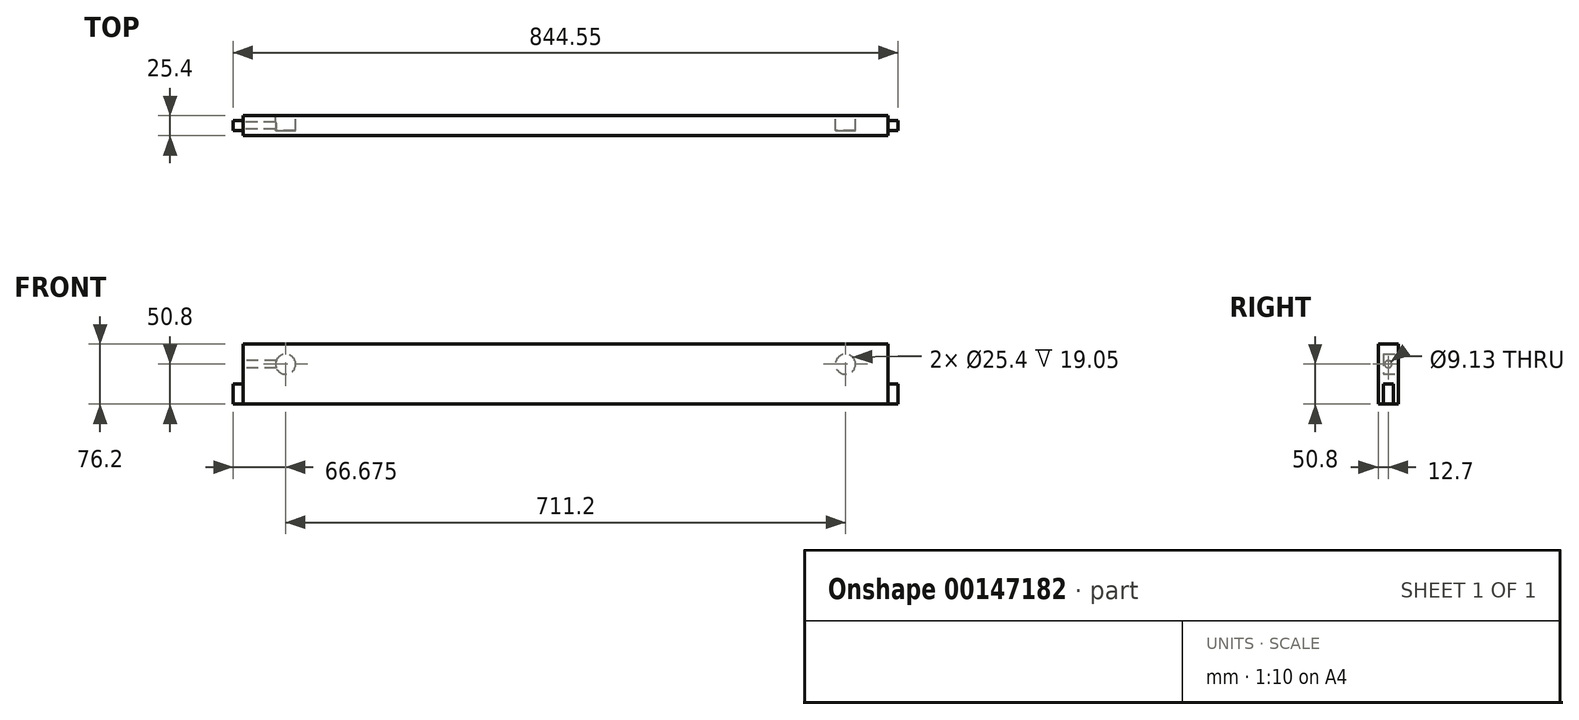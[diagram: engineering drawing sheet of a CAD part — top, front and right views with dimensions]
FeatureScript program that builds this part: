
annotation { "Feature Type Name" : "Feature", "Feature Type Description" : "" }
export const myFeature = defineFeature(function(context is Context, id is Id, definition is map)
    precondition{}
    {
        {
            var Q0;
            Q0=qCreatedBy(makeId("Front.planeOp"),FACE);
            var sketch = newSketch(context, id + "F0", { "sketchPlane" : qUnion([Q0])});
            skLineSegment(sketch, "E0.bottom", {"start": v(0, 0) * mm, "end": v(844.55, 0) * mm});
            skLineSegment(sketch, "E0.top", {"start": v(0, 76.2) * mm, "end": v(844.55, 76.2) * mm});
            skLineSegment(sketch, "E0.left", {"start": v(0, 0) * mm, "end": v(0, 76.2) * mm});
            skLineSegment(sketch, "E0.right", {"start": v(844.55, 0) * mm, "end": v(844.55, 76.2) * mm});
            skSolve(sketch);
        }
        {
            var Q0;
            Q0=makeQuery(id+"F0.imprint","IMPRINT",FACE,{"disambiguationData":[TD([[makeQuery(id+"F0.imprint","IMPRINT",EDGE,{"derivedFrom":sQuery(id+"F0.wireOp",EDGE,"E0.bottom")}),1.0]])]});
            extrude(context, id + "F1", {"entities" : qUnion([Q0]), "depth" : 25.4 * mm});
        }
        {
            var Q0;
            Q0=makeQuery(id+"F1.opExtrude","CAP_FACE",FACE,{"disambiguationData":[OSD([sQuery(id+"F0.wireOp",EDGE,"E0.bottom"),sQuery(id+"F0.wireOp",EDGE,"E0.top"),sQuery(id+"F0.wireOp",EDGE,"E0.left"),sQuery(id+"F0.wireOp",EDGE,"E0.right")])],"isStart":false});
            var sketch = newSketch(context, id + "F2", { "sketchPlane" : qUnion([Q0])});
            skLineSegment(sketch, "E1.bottom", {"start": v(0, 76.2) * mm, "end": v(12.7, 76.2) * mm});
            skLineSegment(sketch, "E1.top", {"start": v(0, 25.4) * mm, "end": v(12.7, 25.4) * mm});
            skLineSegment(sketch, "E1.left", {"start": v(0, 76.2) * mm, "end": v(0, 25.4) * mm});
            skLineSegment(sketch, "E1.right", {"start": v(12.7, 76.2) * mm, "end": v(12.7, 25.4) * mm});
            skLineSegment(sketch, "E2.bottom", {"start": v(831.85, 76.2) * mm, "end": v(844.55, 76.2) * mm});
            skLineSegment(sketch, "E2.top", {"start": v(831.85, 25.4) * mm, "end": v(844.55, 25.4) * mm});
            skLineSegment(sketch, "E2.left", {"start": v(831.85, 76.2) * mm, "end": v(831.85, 25.4) * mm});
            skLineSegment(sketch, "E2.right", {"start": v(844.55, 76.2) * mm, "end": v(844.55, 25.4) * mm});
            skSolve(sketch);
        }
        {
            var Q0;
            Q0=makeQuery(id+"F2.imprint","IMPRINT",FACE,{"disambiguationData":[TD([[makeQuery(id+"F2.imprint","IMPRINT",EDGE,{"derivedFrom":sQuery(id+"F2.wireOp",EDGE,"E1.bottom")}),-1.0]])]});
            var Q1;
            Q1=makeQuery(id+"F2.imprint","IMPRINT",FACE,{"disambiguationData":[TD([[makeQuery(id+"F2.imprint","IMPRINT",EDGE,{"derivedFrom":sQuery(id+"F2.wireOp",EDGE,"E2.bottom")}),-1.0]])]});
            extrude(context, id + "F3", {"entities" : qUnion([Q0, Q1]), "operationType" : NewBodyOperationType.REMOVE, "endBound" : BoundingType.THROUGH_ALL, "oppositeDirection" : true, "depth" : 25.4 * mm});
        }
        {
            var Q0;
            Q0=makeQuery(id+"F1.opExtrude","SWEPT_FACE",FACE,{"disambiguationData":[OSD([sQuery(id+"F0.wireOp",EDGE,"E0.bottom")])]});
            var sketch = newSketch(context, id + "F4", { "sketchPlane" : qUnion([Q0])});
            skLineSegment(sketch, "E3.bottom", {"start": v(0, 25.4) * mm, "end": v(12.7, 25.4) * mm});
            skLineSegment(sketch, "E3.top", {"start": v(0, 19.05) * mm, "end": v(12.7, 19.05) * mm});
            skLineSegment(sketch, "E3.left", {"start": v(0, 25.4) * mm, "end": v(0, 19.05) * mm});
            skLineSegment(sketch, "E3.right", {"start": v(12.7, 25.4) * mm, "end": v(12.7, 19.05) * mm});
            skLineSegment(sketch, "E4.bottom", {"start": v(831.85, 25.4) * mm, "end": v(844.55, 25.4) * mm});
            skLineSegment(sketch, "E4.top", {"start": v(831.85, 19.05) * mm, "end": v(844.55, 19.05) * mm});
            skLineSegment(sketch, "E4.left", {"start": v(831.85, 25.4) * mm, "end": v(831.85, 19.05) * mm});
            skLineSegment(sketch, "E4.right", {"start": v(844.55, 25.4) * mm, "end": v(844.55, 19.05) * mm});
            skLineSegment(sketch, "E5.bottom", {"start": v(0, 6.35) * mm, "end": v(12.7, 6.35) * mm});
            skLineSegment(sketch, "E5.top", {"start": v(0, 0) * mm, "end": v(12.7, 0) * mm});
            skLineSegment(sketch, "E5.left", {"start": v(0, 6.35) * mm, "end": v(0, 0) * mm});
            skLineSegment(sketch, "E5.right", {"start": v(12.7, 6.35) * mm, "end": v(12.7, 0) * mm});
            skLineSegment(sketch, "E6.bottom", {"start": v(831.85, 6.35) * mm, "end": v(844.55, 6.35) * mm});
            skLineSegment(sketch, "E6.top", {"start": v(831.85, 0) * mm, "end": v(844.55, 0) * mm});
            skLineSegment(sketch, "E6.left", {"start": v(831.85, 6.35) * mm, "end": v(831.85, 0) * mm});
            skLineSegment(sketch, "E6.right", {"start": v(844.55, 6.35) * mm, "end": v(844.55, 0) * mm});
            skSolve(sketch);
        }
        {
            var Q0;
            Q0=makeQuery(id+"F4.imprint","IMPRINT",FACE,{"disambiguationData":[TD([[makeQuery(id+"F4.imprint","IMPRINT",EDGE,{"derivedFrom":sQuery(id+"F4.wireOp",EDGE,"E4.bottom")}),-1.0]])]});
            var Q1;
            Q1=makeQuery(id+"F4.imprint","IMPRINT",FACE,{"disambiguationData":[TD([[makeQuery(id+"F4.imprint","IMPRINT",EDGE,{"derivedFrom":sQuery(id+"F4.wireOp",EDGE,"E6.bottom")}),-1.0]])]});
            var Q2;
            Q2=makeQuery(id+"F4.imprint","IMPRINT",FACE,{"disambiguationData":[TD([[makeQuery(id+"F4.imprint","IMPRINT",EDGE,{"derivedFrom":sQuery(id+"F4.wireOp",EDGE,"E3.bottom")}),-1.0]])]});
            var Q3;
            Q3=makeQuery(id+"F4.imprint","IMPRINT",FACE,{"disambiguationData":[TD([[makeQuery(id+"F4.imprint","IMPRINT",EDGE,{"derivedFrom":sQuery(id+"F4.wireOp",EDGE,"E5.bottom")}),-1.0]])]});
            extrude(context, id + "F5", {"entities" : qUnion([Q0, Q1, Q2, Q3]), "operationType" : NewBodyOperationType.REMOVE, "endBound" : BoundingType.THROUGH_ALL, "oppositeDirection" : true, "depth" : 25.4 * mm});
        }
        {
            var Q0;
            Q0=makeQuery(id+"F5.boolean.opBoolean","MERGE",FACE,{"derivedFrom":[makeQuery(id+"F3.boolean.opBoolean","COPY",FACE,{"derivedFrom":makeQuery(id+"F3.opExtrude","SWEPT_FACE",FACE,{"disambiguationData":[OSD([sQuery(id+"F2.wireOp",EDGE,"E1.right")])]})}),makeQuery(id+"F5.opExtrude","SWEPT_FACE",FACE,{"disambiguationData":[OSD([sQuery(id+"F4.wireOp",EDGE,"E3.right")])]}),makeQuery(id+"F5.opExtrude","SWEPT_FACE",FACE,{"disambiguationData":[OSD([sQuery(id+"F4.wireOp",EDGE,"E5.right")])]})]});
            var sketch = newSketch(context, id + "F6", { "sketchPlane" : qUnion([Q0])});
            skCircle(sketch, "E7", {"center": v(12.7, 50.8) * mm, "radius": 4.56 * mm});
            skPoint(sketch, "E7.centerSnap0", {"position": v(12.7, 76.2) * mm});
            skSolve(sketch);
        }
        {
            var Q0;
            Q0=makeQuery(id+"F6.imprint","IMPRINT",FACE,{"disambiguationData":[TD([[makeQuery(id+"F6.imprint","IMPRINT",EDGE,{"derivedFrom":sQuery(id+"F6.wireOp",EDGE,"E7")}),1.0]])]});
            extrude(context, id + "F7", {"entities" : qUnion([Q0]), "operationType" : NewBodyOperationType.REMOVE, "oppositeDirection" : true, "depth" : 50.8 * mm});
        }
        {
            var Q0;
            Q0=makeQuery(id+"F1.opExtrude","CAP_FACE",FACE,{"disambiguationData":[OSD([sQuery(id+"F0.wireOp",EDGE,"E0.bottom"),sQuery(id+"F0.wireOp",EDGE,"E0.top"),sQuery(id+"F0.wireOp",EDGE,"E0.left"),sQuery(id+"F0.wireOp",EDGE,"E0.right")])],"isStart":true});
            var sketch = newSketch(context, id + "F8", { "sketchPlane" : qUnion([Q0])});
            skCircle(sketch, "E8", {"center": v(-66.67, 50.8) * mm, "radius": 12.7 * mm});
            skCircle(sketch, "E9", {"center": v(-777.88, 50.8) * mm, "radius": 12.7 * mm});
            skSolve(sketch);
        }
        {
            var Q0;
            Q0=makeQuery(id+"F8.imprint","IMPRINT",FACE,{"disambiguationData":[TD([[makeQuery(id+"F8.imprint","IMPRINT",EDGE,{"derivedFrom":sQuery(id+"F8.wireOp",EDGE,"E8")}),1.0]])]});
            var Q1;
            Q1=makeQuery(id+"F8.imprint","IMPRINT",FACE,{"disambiguationData":[TD([[makeQuery(id+"F8.imprint","IMPRINT",EDGE,{"derivedFrom":sQuery(id+"F8.wireOp",EDGE,"E9")}),1.0]])]});
            extrude(context, id + "F9", {"entities" : qUnion([Q0, Q1]), "operationType" : NewBodyOperationType.REMOVE, "oppositeDirection" : true, "depth" : 19.05 * mm});
        }
    });
